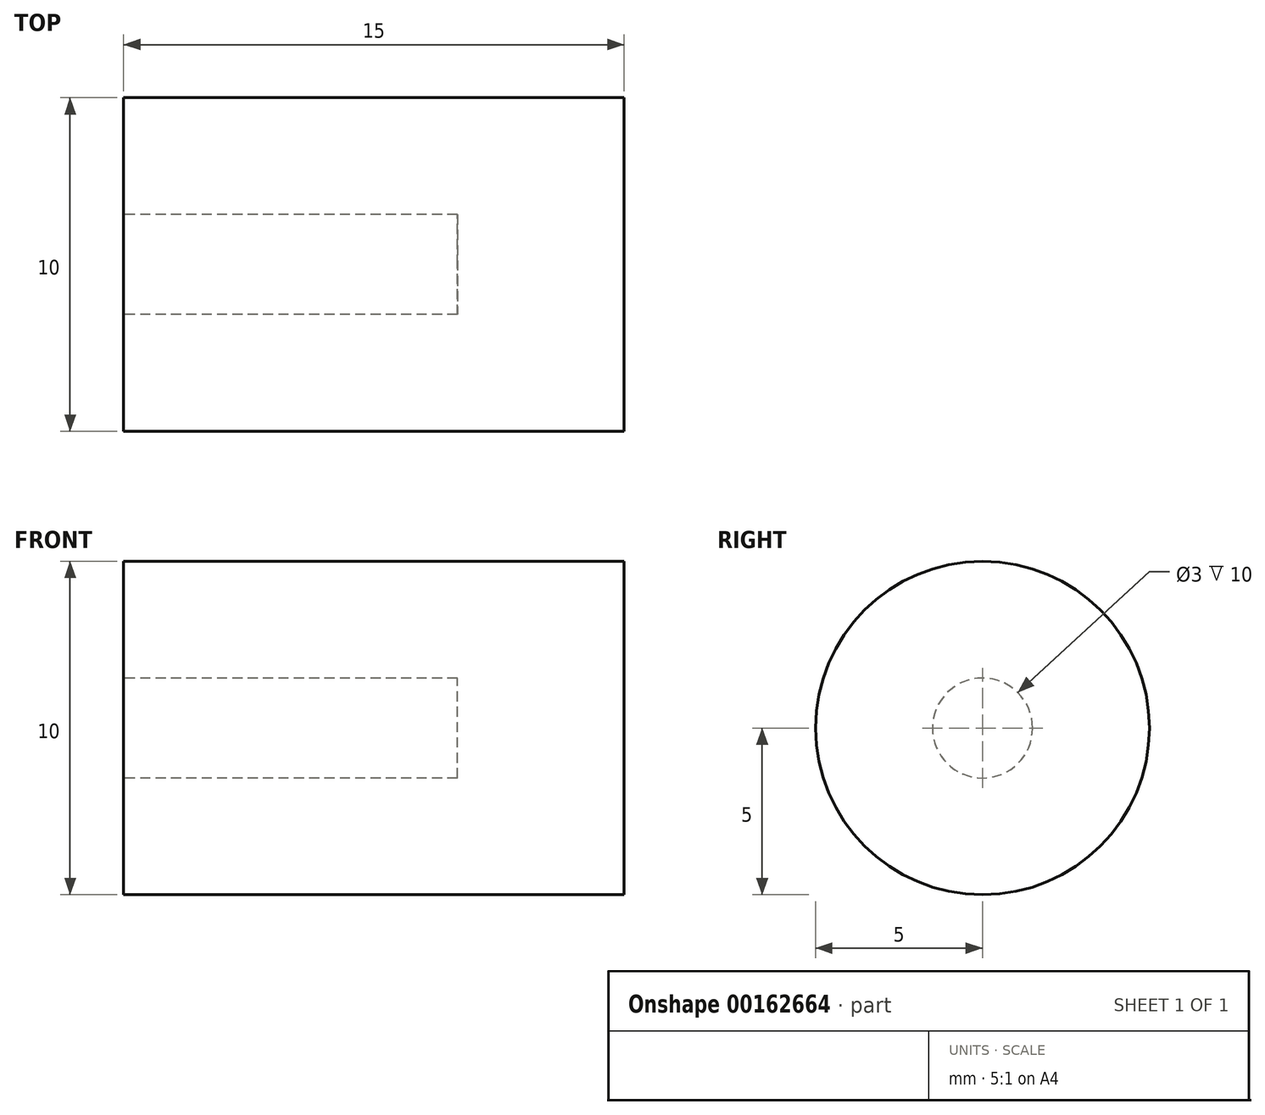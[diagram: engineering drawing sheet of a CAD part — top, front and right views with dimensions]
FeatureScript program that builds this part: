
annotation { "Feature Type Name" : "Feature", "Feature Type Description" : "" }
export const myFeature = defineFeature(function(context is Context, id is Id, definition is map)
    precondition{}
    {
        {
            var Q0;
            Q0=qCreatedBy(makeId("Right.planeOp"),FACE);
            var sketch = newSketch(context, id + "F0", { "sketchPlane" : qUnion([Q0])});
            skCircle(sketch, "E0", {"center": v(0, 0) * mm, "radius": 5 * mm});
            skCircle(sketch, "E1", {"center": v(0, 0) * mm, "radius": 1.5 * mm});
            skSolve(sketch);
        }
        {
            var Q0;
            Q0 = qSketchRegion(id + "F0", true);
            var Q1;
            Q1=makeQuery(id+"F0.imprint","IMPRINT",FACE,{"disambiguationData":[TD([[makeQuery(id+"F0.imprint","IMPRINT",EDGE,{"derivedFrom":sQuery(id+"F0.wireOp",EDGE,"E1")}),1.0]])]});
            extrude(context, id + "F1", {"entities" : qUnion([Q0, Q1]), "depth" : 15 * mm, "offsetDistance" : 25 * mm});
        }
        {
            var Q0;
            Q0=makeQuery(id+"F0.imprint","IMPRINT",FACE,{"disambiguationData":[TD([[makeQuery(id+"F0.imprint","IMPRINT",EDGE,{"derivedFrom":sQuery(id+"F0.wireOp",EDGE,"E1")}),1.0]])]});
            var Q1;
            Q1=sQuery(id+"F0.wireOp",EDGE,"E1");
            extrude(context, id + "F2", {"entities" : qUnion([Q0]), "operationType" : NewBodyOperationType.REMOVE, "surfaceEntities" : qUnion([Q1]), "depth" : 10 * mm, "offsetDistance" : 25 * mm});
        }
    });
